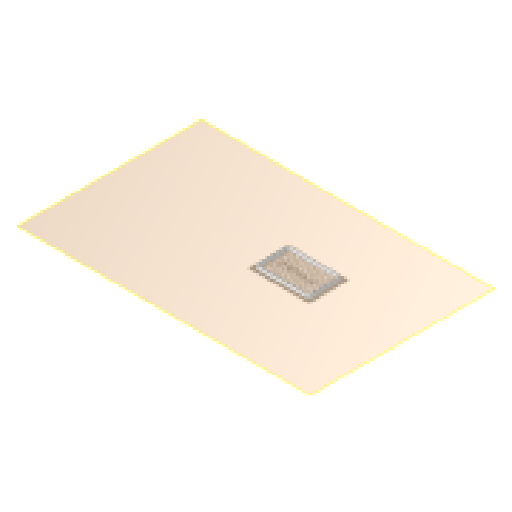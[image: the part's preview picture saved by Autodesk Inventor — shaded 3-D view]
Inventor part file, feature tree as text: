
AUTODESK INVENTOR PART (.ipt)
format: ipt  version: 2024.1 (Build 281209000, 209)  size: 570,368 bytes
history: native  units: mm
features: projected_geometry x13, extrude x4, sketch x4, other x2, plane x1, fillet x1, pattern_linear x1, reference x1
ambient origin geometry x8: Origin, YZ Plane, XZ Plane, XY Plane, X Axis, Y Axis, Z Axis, Center Point
bodies: Volumenkörper1 (feature_tree)
feature tree (27):
  plane  "Arbeitsebene1"
  extrude  "Extrusion1"  Depth=2.0mm
  extrude  "Extrusion2"  Depth=5.0mm
  extrude  "Extrusion3"  Depth=2.0mm
  extrude  "Extrusion4"  Depth=4.0mm
  fillet  "Rundung1"  Radius=1.0mm
  pattern_linear  "Rechteckige Anordnung1"  Spacing1=1.0mm  [1 undecoded]
  sketch  "Skizze1"  dims[d0=0.2mm d1=2.0mm]
  reference  "Referenz1"
  sketch  "Skizze2"  dims[d2=5.0mm d3=-0.872665mm d4=90.0mm]
  projected_geometry  "Projizierte Kontur1"
  projected_geometry  "Projizierte Kontur2"
  projected_geometry  "Projizierte Kontur3"
  projected_geometry  "Projizierte Kontur4"
  sketch  "Skizze3"  dims[d5=60.0mm d6=2.0mm]
  projected_geometry  "Projizierte Kontur5"
  sketch  "Skizze4"  dims[d7=72.0mm d8=42.0mm d9=1.0mm d10=0.0mm d11=1.0mm d12=0.0mm d13=2.0mm d14=2.0mm d15=1.0mm d16=0.0mm d17=0.9mm d18=100.0mm d20=4.0mm]
  projected_geometry  "Projizierte Kontur6"
  projected_geometry  "Projizierte Kontur7"
  projected_geometry  "Projizierte Kontur8"
  projected_geometry  "Projizierte Kontur9"
  projected_geometry  "Projizierte Kontur10"
  projected_geometry  "Projizierte Kontur11"
  projected_geometry  "Projizierte Kontur12"
  projected_geometry  "Projizierte Kontur13"
  other  "Assembly_Planktoscope_Uc2version_wormdrive_V3.iam"
  other  "BoxCotout:1"
note: 1 required parameter value undecoded (feature->parameter linkage not recoverable at this tier; creation-order binding heuristic only, values carry confidence <= 0.55)
